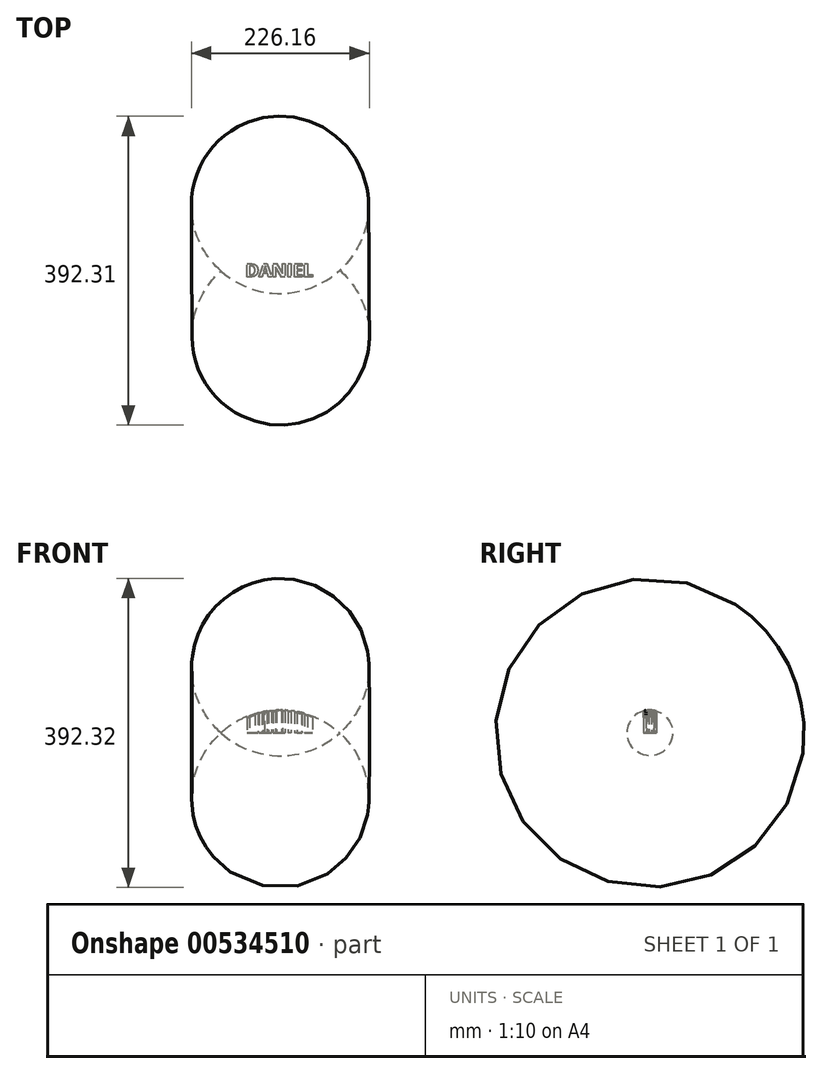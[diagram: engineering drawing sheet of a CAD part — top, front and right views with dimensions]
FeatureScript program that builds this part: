
annotation { "Feature Type Name" : "Feature", "Feature Type Description" : "" }
export const myFeature = defineFeature(function(context is Context, id is Id, definition is map)
    precondition{}
    {
        {
            var Q0;
            Q0=qCreatedBy(makeId("Top.planeOp"),FACE);
            var sketch = newSketch(context, id + "F0", { "sketchPlane" : qUnion([Q0])});
            skArc(sketch, "E0", {"start": v(-74.53, -0.85) * mm, "mid": v(1.14, -29.5) * mm, "end": v(76.49, 0) * mm});
            skLineSegment(sketch, "E1", {"start": v(-74.53, -0.85) * mm, "end": v(76.49, 0) * mm});
            skSolve(sketch);
        }
        {
            var Q0;
            Q0=makeQuery(id+"F0.imprint","IMPRINT",FACE,{"disambiguationData":[TD([[makeQuery(id+"F0.imprint","IMPRINT",EDGE,{"derivedFrom":sQuery(id+"F0.wireOp",EDGE,"E0")}),1.0]])]});
            var Q1;
            Q1=sQuery(id+"F0.wireOp",EDGE,"E1");
            revolve(context, id + "F1", {"entities" : qUnion([Q0]), "axis" : qUnion([Q1]), "revolveType" : RevolveType.FULL});
        }
        {
            var Q0;
            Q0=qCreatedBy(makeId("Top.planeOp"),FACE);
            var sketch = newSketch(context, id + "F2", { "sketchPlane" : qUnion([Q0])});
            skText(sketch, "E2", { "text": "DANIEL", "fontName": "OpenSans-Bold.ttf"});
            const initialGuessF2  = {"E2": [-0.04353, -0.00841, 1, 0, 0.01682]};
            skSetInitialGuess(sketch, initialGuessF2);
            skSolve(sketch);
        }
        {
            var Q0;
            Q0 = qSketchRegion(id + "F2", true);
            extrude(context, id + "F3", {"entities" : qUnion([Q0]), "operationType" : NewBodyOperationType.REMOVE, "endBound" : BoundingType.UP_TO_NEXT, "depth" : 25.4 * mm, "offsetDistance" : 25.4 * mm});
        }
    });
